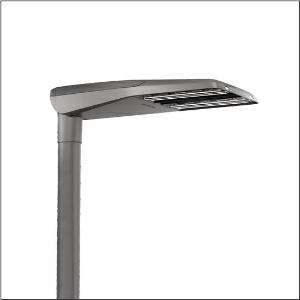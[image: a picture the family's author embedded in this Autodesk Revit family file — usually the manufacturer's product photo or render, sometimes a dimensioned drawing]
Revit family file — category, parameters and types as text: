
# Revit family: streetlight_sl_11_iq_midi___st1_2p1_0_5xc3g51f08me_c537
name_source: partatom
category: Lighting Fixtures
units: mm (PartAtom-declared; Revit-internal decimal feet)

## family parameters
Cut with Voids When Loaded = No
Host = Face
Light Source = No
Part Type = Normal
Room Calculation Point = No
Round Connector Dimension = Use Diameter
Shared = No

## types (1)
- --- (1 x LED, 17750 lm, 124.7 W, 3000K)
    Apparent Load = 125 VA
    CIE Flux Codes = 31 68 95 100 100
    Color Rendering = 70
    Color Temperature = 3000K
    Default Elevation = 1800 mm
    Description = Streetlight SL 11 iQ midi, mast luminaire, primary light control with 3 zone facetted reflector, of plastic, silver coated, highly specular, primary optical cover: cover, of PMMA, transparent, light distribution: ST1.2P1.0, light emission: direct distribution, primary light characteristic: asymmetric, installation type: post-top, side-entry, LED, High Power LED, rated luminous flux: 17.750lm, luminous efficacy: 142lm/W, light colour: 730, colour temperature: 3000K, control: Street-Remote, optimised constant luminous flux control (CLO 2.0), Auto-Match, Desk-Remote (wireless, voltage-free reading and setting of iQ features in the workshop via application-optimized NFC function/RFID function), Light-Fading, Smart-Wire, Night-Set, Lumen-Switch, Temp-Guard, with cable H07RN-F 5x 1.5mm², mains connection: 230..240V, AC, 50/60Hz, connection cable pre-assembled, cable length: 12,5m, start of lifetime: 125W, end of service life: 132W, reduction: 57W, luminaire housing, of diecast aluminium, powder-coated, Siteco® metallic grey (DB 702S), please order mast flange separately, inclination adjustable without tools: 0°, 5°, 10°, 15° (post-top) | 0°, -5°, -10°, -15° (side-entry), sealing non-destructively replaceable, multi-level sealing system, length: 780mm, width: 376mm, height: 118mm, mast flange for spigot size: 42mm (side-entry): 5XC10008XM4, 60/48mm (side-entry/post-top): 5XC10108XM2, 76/60mm (side-entry/post-top): 5XC10108XM1, equipment: Power, protection rating (complete): IP66, insulation class (complete): insulation class II (safety insulation), certification: CE, ENEC, VDE, impact resistance: IK09, permissible operating ambient temperature for outdoor applications: -25..+50°C, standard-compliant lighting for roads and squares, Environmental Product Declaration (EPD) tested and certified by an independent institute, packaging unit: 1 piece

Light Distribution: ST1.2P1.0
    Height = 118 mm
    Lamp = 1 x LED
    Lamp Light Flux = 17750 lm
    Lamp Power = 124.7 W
    Lamp count = 1
    Length = 780 mm
    Luminous efficacy = 142 lm/W
    Manufacturer = Siteco
    ModVariant = No
    Model = 5XC3G51F08ME
    Number of Poles = 1
    OnlyDefault = Yes
    Power Factor = 1
    Product Name = Streetlight SL 11 iQ midi | ST1.2P1.0
    Product group = mast luminaire | pylon top
    ProductGroupID = 6100
    Protection Class = Protection class II
    Protection Degree = IP 66
    RLX_Detail_Level = 1
    RLX_Emergency_Light_Flux = 0 lm
    RLX_Emergency_Type = 0
    RLX_Emergency_Type_DB = No
    RlxData = <blob elided: 70665 chars, md5=cc20c53c>
    Socket = socket
    Standby Power = 0 W
    System Light Flux = 17750 lm
    System Power = 125 W
    Type Comments = factory setting: luminous flux: 100 % | dim-lin: 254 | 557 mA
    Type Image = l_1005960.jpg
    URL = http://relux.com
    VarID = @adj_129497
    Voltage = 0 V
    Weight = 0.00 kg
    Width = 376 mm

## geometry (parser evidence)
native form markers: Blend x4, Sweep x9
no freeform markers — native parametric forms only
